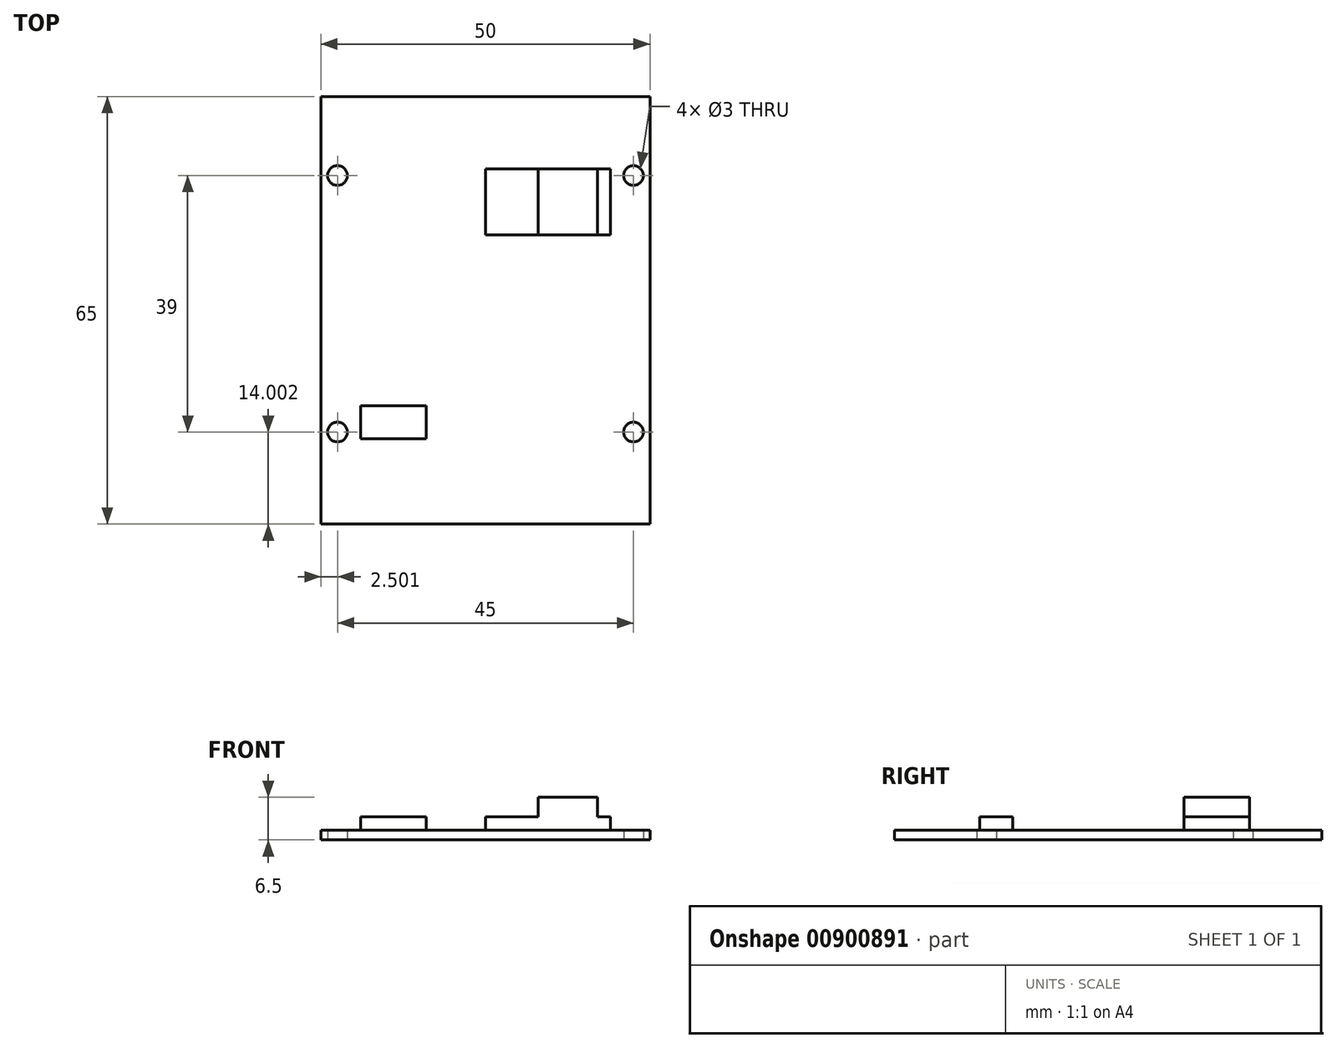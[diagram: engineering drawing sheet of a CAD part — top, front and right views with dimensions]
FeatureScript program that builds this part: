
annotation { "Feature Type Name" : "Feature", "Feature Type Description" : "" }
export const myFeature = defineFeature(function(context is Context, id is Id, definition is map)
    precondition{}
    {
        {
            var Q0;
            Q0=qCreatedBy(makeId("Top.planeOp"),FACE);
            var sketch = newSketch(context, id + "F0", { "sketchPlane" : qUnion([Q0])});
            skLineSegment(sketch, "E0.bottom", {"start": v(-23.74, -20.67) * mm, "end": v(26.26, -20.67) * mm});
            skLineSegment(sketch, "E0.top", {"start": v(-23.74, 44.33) * mm, "end": v(26.26, 44.33) * mm});
            skLineSegment(sketch, "E0.left", {"start": v(-23.74, -20.67) * mm, "end": v(-23.74, 44.33) * mm});
            skLineSegment(sketch, "E0.right", {"start": v(26.26, -20.67) * mm, "end": v(26.26, 44.33) * mm});
            skLineSegment(sketch, "E1", {"start": v(23.76, 44.33) * mm, "end": v(23.76, 32.33) * mm, "construction": true});
            skCircle(sketch, "E2", {"center": v(23.76, 32.33) * mm, "radius": 1.5 * mm});
            skLineSegment(sketch, "E3", {"start": v(23.76, 32.33) * mm, "end": v(26.26, 32.33) * mm, "construction": true});
            skLineSegment(sketch, "E4.MirrorCS", {"start": v(-21.24, 44.33) * mm, "end": v(-21.24, 32.33) * mm, "construction": true});
            skCircle(sketch, "E5.MirrorC", {"center": v(-21.24, 32.33) * mm, "radius": 1.5 * mm});
            skLineSegment(sketch, "E6.MirrorCS", {"start": v(-21.24, 32.33) * mm, "end": v(-23.74, 32.33) * mm, "construction": true});
            skLineSegment(sketch, "E7", {"start": v(23.76, -20.67) * mm, "end": v(23.76, -6.67) * mm, "construction": true});
            skLineSegment(sketch, "E8", {"start": v(23.76, -6.67) * mm, "end": v(26.26, -6.67) * mm, "construction": true});
            skCircle(sketch, "E9", {"center": v(23.76, -6.67) * mm, "radius": 1.5 * mm});
            skLineSegment(sketch, "E10", {"start": v(1.26, -20.67) * mm, "end": v(1.26, 44.33) * mm, "construction": true});
            skLineSegment(sketch, "E11.MirrorCS", {"start": v(-21.24, -6.67) * mm, "end": v(-23.74, -6.67) * mm, "construction": true});
            skCircle(sketch, "E12.MirrorC", {"center": v(-21.24, -6.67) * mm, "radius": 1.5 * mm});
            skLineSegment(sketch, "E13.MirrorCS", {"start": v(-21.24, -20.67) * mm, "end": v(-21.24, -6.67) * mm, "construction": true});
            skSolve(sketch);
        }
        {
            var Q0;
            Q0=makeQuery(id+"F0.imprint","IMPRINT",FACE,{"disambiguationData":[TD([[makeQuery(id+"F0.imprint","IMPRINT",EDGE,{"derivedFrom":sQuery(id+"F0.wireOp",EDGE,"E0.bottom")}),1.0]])]});
            extrude(context, id + "F1", {"entities" : qUnion([Q0]), "depth" : 1.5 * mm, "offsetDistance" : 25 * mm});
        }
        {
            var Q0;
            Q0=makeQuery(id+"F1.opExtrude","CAP_FACE",FACE,{"disambiguationData":[OSD([sQuery(id+"F0.wireOp",EDGE,"E0.bottom"),sQuery(id+"F0.wireOp",EDGE,"E0.top"),sQuery(id+"F0.wireOp",EDGE,"E0.left"),sQuery(id+"F0.wireOp",EDGE,"E0.right"),sQuery(id+"F0.wireOp",EDGE,"E2"),sQuery(id+"F0.wireOp",EDGE,"E5.MirrorC"),sQuery(id+"F0.wireOp",EDGE,"E9"),sQuery(id+"F0.wireOp",EDGE,"E12.MirrorC")])],"isStart":false});
            var sketch = newSketch(context, id + "F2", { "sketchPlane" : qUnion([Q0])});
            skLineSegment(sketch, "E14.bottom", {"start": v(20.26, 33.33) * mm, "end": v(1.26, 33.33) * mm});
            skLineSegment(sketch, "E14.top", {"start": v(20.26, 23.33) * mm, "end": v(1.26, 23.33) * mm});
            skLineSegment(sketch, "E14.left", {"start": v(20.26, 33.33) * mm, "end": v(20.26, 23.33) * mm});
            skLineSegment(sketch, "E14.right", {"start": v(1.26, 33.33) * mm, "end": v(1.26, 23.33) * mm});
            skLineSegment(sketch, "E15.bottom", {"start": v(9.26, 33.33) * mm, "end": v(18.26, 33.33) * mm});
            skLineSegment(sketch, "E15.top", {"start": v(9.26, 23.33) * mm, "end": v(18.26, 23.33) * mm});
            skLineSegment(sketch, "E15.left", {"start": v(9.26, 33.33) * mm, "end": v(9.26, 23.33) * mm});
            skLineSegment(sketch, "E15.right", {"start": v(18.26, 33.33) * mm, "end": v(18.26, 23.33) * mm});
            skLineSegment(sketch, "E16.bottom", {"start": v(-17.74, -2.67) * mm, "end": v(-7.74, -2.67) * mm});
            skLineSegment(sketch, "E16.top", {"start": v(-17.74, -7.67) * mm, "end": v(-7.74, -7.67) * mm});
            skLineSegment(sketch, "E16.left", {"start": v(-17.74, -2.67) * mm, "end": v(-17.74, -7.67) * mm});
            skLineSegment(sketch, "E16.right", {"start": v(-7.74, -2.67) * mm, "end": v(-7.74, -7.67) * mm});
            skSolve(sketch);
        }
        {
            var Q0;
            Q0=makeQuery(id+"F2.imprint","IMPRINT",FACE,{"disambiguationData":[TD([[makeQuery(id+"F2.imprint","IMPRINT",EDGE,{"derivedFrom":sQuery(id+"F2.wireOp",EDGE,"E16.bottom")}),-1.0]])]});
            extrude(context, id + "F3", {"entities" : qUnion([Q0]), "operationType" : NewBodyOperationType.ADD, "depth" : 2 * mm, "offsetDistance" : 25 * mm});
        }
        {
            var Q0;
            {var subQ2=sQuery(id+"F2.wireOp",EDGE,"E15.left");Q0=makeQuery(id+"F2.imprint","IMPRINT",FACE,{"disambiguationData":[TD([[makeQuery(id+"F2.imprint","IMPRINT",EDGE,{"derivedFrom":subQ2}),1.0]])]});}
            extrude(context, id + "F4", {"entities" : qUnion([Q0]), "operationType" : NewBodyOperationType.ADD, "depth" : 5 * mm, "offsetDistance" : 25 * mm});
        }
        {
            var Q0;
            {var subQ2=sQuery(id+"F2.wireOp",EDGE,"E14.left");Q0=makeQuery(id+"F2.imprint","IMPRINT",FACE,{"disambiguationData":[TD([[makeQuery(id+"F2.imprint","IMPRINT",EDGE,{"derivedFrom":subQ2}),-1.0]])]});}
            var Q1;
            {var subQ0=sQuery(id+"F2.wireOp",EDGE,"E14.right");Q1=makeQuery(id+"F2.imprint","IMPRINT",FACE,{"disambiguationData":[TD([[makeQuery(id+"F2.imprint","IMPRINT",EDGE,{"derivedFrom":subQ0}),1.0]])]});}
            extrude(context, id + "F5", {"entities" : qUnion([Q0, Q1]), "operationType" : NewBodyOperationType.ADD, "depth" : 2 * mm, "offsetDistance" : 25 * mm});
        }
    });
